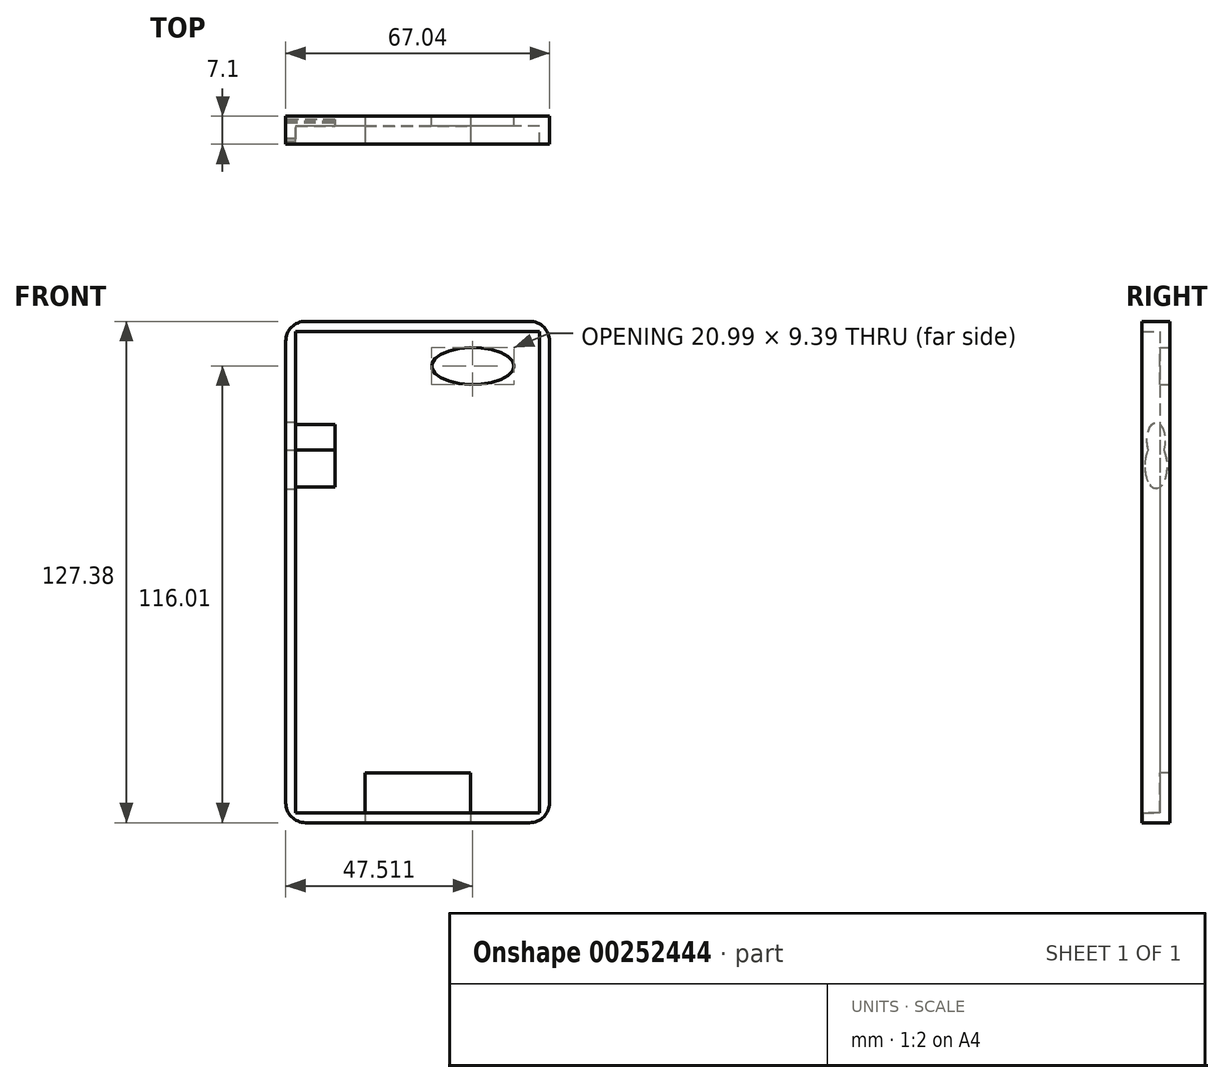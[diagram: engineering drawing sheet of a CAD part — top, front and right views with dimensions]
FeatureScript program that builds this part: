
annotation { "Feature Type Name" : "Feature", "Feature Type Description" : "" }
export const myFeature = defineFeature(function(context is Context, id is Id, definition is map)
    precondition{}
    {
        {
            var Q0;
            Q0=qCreatedBy(makeId("Front.planeOp"),FACE);
            var sketch = newSketch(context, id + "F0", { "sketchPlane" : qUnion([Q0])});
            skLineSegment(sketch, "E0.bottom", {"start": v(33.52, 63.69) * mm, "end": v(-33.52, 63.69) * mm});
            skLineSegment(sketch, "E0.top", {"start": v(33.52, -63.69) * mm, "end": v(-33.52, -63.69) * mm});
            skLineSegment(sketch, "E0.left", {"start": v(33.52, 63.69) * mm, "end": v(33.52, -63.69) * mm});
            skLineSegment(sketch, "E0.right", {"start": v(-33.52, 63.69) * mm, "end": v(-33.52, -63.69) * mm});
            skPoint(sketch, "E0.middle", {"position": v(0, 0) * mm});
            skSolve(sketch);
        }
        {
            var Q0;
            Q0 = qSketchRegion(id + "F0", true);
            extrude(context, id + "F1", {"entities" : qUnion([Q0]), "endBound" : BoundingType.SYMMETRIC, "depth" : 7.1 * mm});
        }
        {
            var Q0;
            Q0=makeQuery(id+"F1.opExtrude","CAP_FACE",FACE,{"disambiguationData":[OSD([sQuery(id+"F0.wireOp",EDGE,"E0.bottom"),sQuery(id+"F0.wireOp",EDGE,"E0.top"),sQuery(id+"F0.wireOp",EDGE,"E0.left"),sQuery(id+"F0.wireOp",EDGE,"E0.right")])],"isStart":false});
            shell(context, id + "F2", {"entities" : qUnion([Q0]), "thickness" : 2.54 * mm});
        }
        {
            var Q0;
            Q0=makeQuery(id+"F1.opExtrude","SWEPT_EDGE",EDGE,{"disambiguationData":[OSD([sQuery(id+"F0.wireOp",EDGE,"E0.top"),sQuery(id+"F0.wireOp",EDGE,"E0.left")])]});
            var Q1;
            Q1=makeQuery(id+"F1.opExtrude","SWEPT_EDGE",EDGE,{"disambiguationData":[OSD([sQuery(id+"F0.wireOp",EDGE,"E0.top"),sQuery(id+"F0.wireOp",EDGE,"E0.right")])]});
            var Q2;
            Q2=makeQuery(id+"F1.opExtrude","SWEPT_EDGE",EDGE,{"disambiguationData":[OSD([sQuery(id+"F0.wireOp",EDGE,"E0.bottom"),sQuery(id+"F0.wireOp",EDGE,"E0.right")])]});
            var Q3;
            Q3=makeQuery(id+"F1.opExtrude","SWEPT_EDGE",EDGE,{"disambiguationData":[OSD([sQuery(id+"F0.wireOp",EDGE,"E0.bottom"),sQuery(id+"F0.wireOp",EDGE,"E0.left")])]});
            fillet(context, id + "F3", {"entities" : qUnion([Q0, Q1, Q2, Q3]), "radius" : 5.08 * mm, "tangentPropagation" : true, "allowEdgeOverflow" : false});
        }
        {
            var Q0;
            Q0=makeQuery(id+"F2.opShell","OFFSET_FACE",FACE,{"disambiguationData":[OSD([sQuery(id+"F0.wireOp",EDGE,"E0.bottom"),sQuery(id+"F0.wireOp",EDGE,"E0.top"),sQuery(id+"F0.wireOp",EDGE,"E0.left"),sQuery(id+"F0.wireOp",EDGE,"E0.right")])]});
            var sketch = newSketch(context, id + "F4", { "sketchPlane" : qUnion([Q0])});
            skSolve(sketch);
        }
        {
            var Q0;
            {var subQ0=sQuery(id+"F0.wireOp",EDGE,"E0.bottom");Q0=makeQuery(id+"F4.imprint","IMPRINT",FACE,{"disambiguationData":[TD([[makeQuery(id+"F4.imprint","IMPRINT",EDGE,{"derivedFrom":makeQuery(id+"F2.opShell","OFFSET_EDGE",EDGE,{"disambiguationData":[OSD([subQ0]),TDD([makeQuery(id+"F1.opExtrude","CAP_EDGE",EDGE,{"disambiguationData":[OSD([subQ0])],"isStart":true})])]})}),1.0]])]});}
            var sketch = newSketch(context, id + "F5", { "sketchPlane" : qUnion([Q0])});
            skEllipse(sketch, "E1", {"center": v(14, 52.32) * mm, "majorRadius": 10.5 * mm, "minorRadius": 4.7 * mm, "majorAxis": v(1, 0)});
            skSolve(sketch);
        }
        {
            var Q0;
            Q0 = qSketchRegion(id + "F5", true);
            var Q1;
            Q1=sQuery(id+"F5.wireOp",EDGE,"E1");
            extrude(context, id + "F6", {"entities" : qUnion([Q0]), "operationType" : NewBodyOperationType.REMOVE, "surfaceEntities" : qUnion([Q1]), "endBound" : BoundingType.SYMMETRIC, "depth" : 25.4 * mm});
        }
        {
            var Q0;
            Q0=makeQuery(id+"F1.opExtrude","SWEPT_FACE",FACE,{"disambiguationData":[OSD([sQuery(id+"F0.wireOp",EDGE,"E0.top")])]});
            var sketch = newSketch(context, id + "F7", { "sketchPlane" : qUnion([Q0])});
            skLineSegment(sketch, "E2.bottom", {"start": v(13.4, -3.35) * mm, "end": v(-13.4, -3.35) * mm});
            skLineSegment(sketch, "E2.top", {"start": v(13.4, 3.35) * mm, "end": v(-13.4, 3.35) * mm});
            skLineSegment(sketch, "E2.left", {"start": v(13.4, -3.35) * mm, "end": v(13.4, 3.35) * mm});
            skLineSegment(sketch, "E2.right", {"start": v(-13.4, -3.35) * mm, "end": v(-13.4, 3.35) * mm});
            skPoint(sketch, "E2.middle", {"position": v(0, 0) * mm});
            skSolve(sketch);
        }
        {
            var Q0;
            Q0=makeQuery(id+"F7.imprint","IMPRINT",FACE,{"disambiguationData":[TD([[makeQuery(id+"F7.imprint","IMPRINT",EDGE,{"derivedFrom":sQuery(id+"F7.wireOp",EDGE,"E2.bottom")}),-1.0]])]});
            extrude(context, id + "F8", {"entities" : qUnion([Q0]), "operationType" : NewBodyOperationType.REMOVE, "endBound" : BoundingType.SYMMETRIC, "oppositeDirection" : true, "depth" : 25.4 * mm});
        }
        {
            var Q0;
            Q0=makeQuery(id+"F1.opExtrude","SWEPT_FACE",FACE,{"disambiguationData":[OSD([sQuery(id+"F0.wireOp",EDGE,"E0.right")])]});
            var sketch = newSketch(context, id + "F9", { "sketchPlane" : qUnion([Q0])});
            skEllipse(sketch, "E3", {"center": v(0, 33.42) * mm, "majorRadius": 4.5 * mm, "minorRadius": 2.31 * mm, "majorAxis": v(0, -1)});
            skSolve(sketch);
        }
        {
            var Q0;
            Q0=makeQuery(id+"F9.imprint","IMPRINT",FACE,{"disambiguationData":[TD([[makeQuery(id+"F9.imprint","IMPRINT",EDGE,{"derivedFrom":sQuery(id+"F9.wireOp",EDGE,"E3")}),1.0]])]});
            extrude(context, id + "F10", {"entities" : qUnion([Q0]), "operationType" : NewBodyOperationType.REMOVE, "endBound" : BoundingType.SYMMETRIC, "depth" : 25 * mm});
        }
        {
            var Q0;
            Q0=makeQuery(id+"F1.opExtrude","SWEPT_FACE",FACE,{"disambiguationData":[OSD([sQuery(id+"F0.wireOp",EDGE,"E0.right")])]});
            var sketch = newSketch(context, id + "F11", { "sketchPlane" : qUnion([Q0])});
            skEllipse(sketch, "E4", {"center": v(0, 26.9) * mm, "majorRadius": 5.76 * mm, "minorRadius": 2.75 * mm, "majorAxis": v(0, -1)});
            skSolve(sketch);
        }
        {
            var Q0;
            Q0=makeQuery(id+"F11.imprint","IMPRINT",FACE,{"disambiguationData":[TD([[makeQuery(id+"F11.imprint","IMPRINT",EDGE,{"derivedFrom":sQuery(id+"F11.wireOp",EDGE,"E4")}),1.0]])]});
            extrude(context, id + "F12", {"entities" : qUnion([Q0]), "operationType" : NewBodyOperationType.REMOVE, "endBound" : BoundingType.SYMMETRIC, "depth" : 25 * mm});
        }
    });
